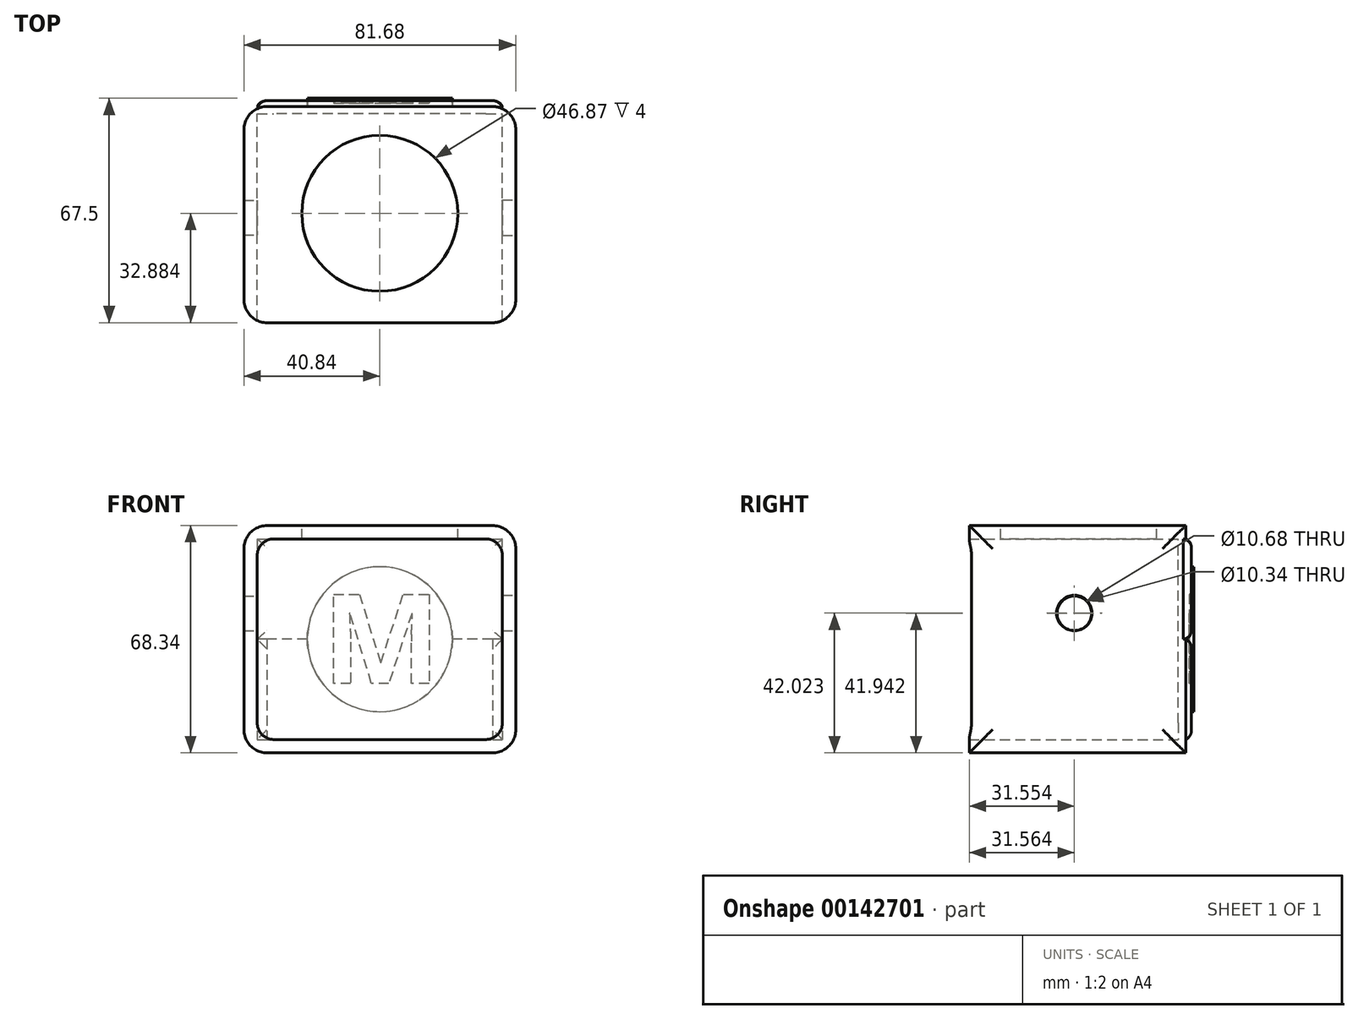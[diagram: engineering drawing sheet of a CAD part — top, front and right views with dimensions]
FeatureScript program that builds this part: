
annotation { "Feature Type Name" : "Feature", "Feature Type Description" : "" }
export const myFeature = defineFeature(function(context is Context, id is Id, definition is map)
    precondition{}
    {
        {
            var Q0;
            Q0=qCreatedBy(makeId("Front.planeOp"),FACE);
            var sketch = newSketch(context, id + "F0", { "sketchPlane" : qUnion([Q0])});
            skLineSegment(sketch, "E0.bottom", {"start": v(-40.84, 34.17) * mm, "end": v(40.84, 34.17) * mm});
            skLineSegment(sketch, "E0.top", {"start": v(-40.84, -34.17) * mm, "end": v(40.84, -34.17) * mm});
            skLineSegment(sketch, "E0.left", {"start": v(-40.84, 34.17) * mm, "end": v(-40.84, -34.17) * mm});
            skLineSegment(sketch, "E0.right", {"start": v(40.84, 34.17) * mm, "end": v(40.84, -34.17) * mm});
            skPoint(sketch, "E0.middle", {"position": v(0, 0) * mm});
            skText(sketch, "E1", { "text": "M", "fontName": "OpenSans-Bold.ttf"});
            skCircle(sketch, "E2", {"center": v(0, 0) * mm, "radius": 21.78 * mm});
            skLineSegment(sketch, "E3.0", {"start": v(-36.84, 30.17) * mm, "end": v(36.84, 30.17) * mm});
            skLineSegment(sketch, "E3.1", {"start": v(-36.84, 30.17) * mm, "end": v(-36.84, -30.17) * mm});
            skLineSegment(sketch, "E3.2", {"start": v(-36.84, -30.17) * mm, "end": v(36.84, -30.17) * mm});
            skLineSegment(sketch, "E3.3", {"start": v(36.84, 30.17) * mm, "end": v(36.84, -30.17) * mm});
            skLineSegment(sketch, "E4", {"start": v(36.84, 0) * mm, "end": v(21.78, 0) * mm});
            skLineSegment(sketch, "E5", {"start": v(-21.78, 0) * mm, "end": v(-36.84, 0) * mm});
            skLineSegment(sketch, "E6.0", {"start": v(36.3, 1.33) * mm, "end": v(21.78, 1.33) * mm});
            skLineSegment(sketch, "E7.MirrorCS", {"start": v(-36.3, 1.33) * mm, "end": v(-21.78, 1.33) * mm});
            skPoint(sketch, "E8", {"position": v(36.84, 0) * mm});
            skPoint(sketch, "E9", {"position": v(21.78, 0) * mm});
            const initialGuessF0  = {"E1": [-0.01722, -0.01329, 1, 0, 0.02702]};
            skSetInitialGuess(sketch, initialGuessF0);
            skSolve(sketch);
        }
        {
            var Q0;
            Q0=makeQuery(id+"F0.imprint","IMPRINT",FACE,{"disambiguationData":[TD([[makeQuery(id+"F0.imprint","IMPRINT",EDGE,{"derivedFrom":sQuery(id+"F0.wireOp",EDGE,"E1.sketch_text.stroke-0")}),1.0]])]});
            var Q1;
            Q1=makeQuery(id+"F0.imprint","IMPRINT",FACE,{"disambiguationData":[TD([[makeQuery(id+"F0.imprint","IMPRINT",EDGE,{"derivedFrom":sQuery(id+"F0.wireOp",EDGE,"E1.sketch_text.stroke-0")}),-1.0]])]});
            var Q2;
            {var subQ7=sQuery(id+"F0.wireOp",EDGE,"E0.bottom");Q2=makeQuery(id+"F0.imprint","IMPRINT",FACE,{"disambiguationData":[TD([[makeQuery(id+"F0.imprint","IMPRINT",EDGE,{"derivedFrom":subQ7}),-1.0]])]});}
            var Q3;
            {var subQ6=sQuery(id+"F0.wireOp",EDGE,"E0.top");Q3=makeQuery(id+"F0.imprint","IMPRINT",FACE,{"disambiguationData":[TD([[makeQuery(id+"F0.imprint","IMPRINT",EDGE,{"derivedFrom":subQ6}),1.0]])]});}
            var Q4;
            {var subQ0=sQuery(id+"F0.wireOp",EDGE,"E3.2");Q4=makeQuery(id+"F0.imprint","IMPRINT",FACE,{"disambiguationData":[TD([[makeQuery(id+"F0.imprint","IMPRINT",EDGE,{"derivedFrom":subQ0}),1.0]])]});}
            var Q5;
            {var subQ0=sQuery(id+"F0.wireOp",EDGE,"E3.0");Q5=makeQuery(id+"F0.imprint","IMPRINT",FACE,{"disambiguationData":[TD([[makeQuery(id+"F0.imprint","IMPRINT",EDGE,{"derivedFrom":subQ0}),-1.0]])]});}
            extrude(context, id + "F1", {"entities" : qUnion([Q0, Q1, Q2, Q3, Q4, Q5]), "depth" : 2.22 * mm});
        }
        {
            var Q0;
            Q0 = qSketchRegion(id + "F0", true);
            extrude(context, id + "F2", {"entities" : qUnion([Q0]), "operationType" : NewBodyOperationType.ADD, "depth" : 65 * mm});
        }
        {
            var Q0;
            Q0=makeQuery(id+"F0.imprint","IMPRINT",FACE,{"disambiguationData":[TD([[makeQuery(id+"F0.imprint","IMPRINT",EDGE,{"derivedFrom":sQuery(id+"F0.wireOp",EDGE,"E1.sketch_text.stroke-0")}),-1.0]])]});
            extrude(context, id + "F3", {"entities" : qUnion([Q0]), "operationType" : NewBodyOperationType.ADD, "oppositeDirection" : true, "depth" : 1 * mm});
        }
        {
            var Q0;
            Q0=makeQuery(id+"F0.imprint","IMPRINT",FACE,{"disambiguationData":[TD([[makeQuery(id+"F0.imprint","IMPRINT",EDGE,{"derivedFrom":sQuery(id+"F0.wireOp",EDGE,"E1.sketch_text.stroke-0")}),1.0]])]});
            extrude(context, id + "F4", {"entities" : qUnion([Q0]), "operationType" : NewBodyOperationType.ADD, "oppositeDirection" : true, "depth" : 2.5 * mm});
        }
        {
            var Q0;
            {var subQ3=sQuery(id+"F0.wireOp",EDGE,"E3.0");Q0=makeQuery(id+"F0.imprint","IMPRINT",FACE,{"disambiguationData":[TD([[makeQuery(id+"F0.imprint","IMPRINT",EDGE,{"derivedFrom":subQ3}),-1.0]])]});}
            var Q1;
            Q1=sQuery(id+"F0.wireOp",EDGE,"E4");
            var Q2;
            Q2=sQuery(id+"F0.wireOp",EDGE,"E5");
            extrude(context, id + "F5", {"entities" : qUnion([Q0]), "operationType" : NewBodyOperationType.ADD, "surfaceEntities" : qUnion([Q1, Q2]), "oppositeDirection" : true, "depth" : 1.75 * mm});
        }
        {
            var Q0;
            {var subQ0=sQuery(id+"F0.wireOp",EDGE,"E0.right");var subQ1=sQuery(id+"F0.wireOp",EDGE,"E0.bottom");Q0=makeQuery(id+"F2.boolean.opBoolean","MERGE",EDGE,{"derivedFrom":[makeQuery(id+"F1.opExtrude","SWEPT_EDGE",EDGE,{"disambiguationData":[OSD([subQ1,subQ0])]}),makeQuery(id+"F2.opExtrude","SWEPT_EDGE",EDGE,{"disambiguationData":[OSD([subQ1,subQ0])]})]});}
            var Q1;
            {var subQ0=sQuery(id+"F0.wireOp",EDGE,"E0.left");var subQ1=sQuery(id+"F0.wireOp",EDGE,"E0.bottom");Q1=makeQuery(id+"F2.boolean.opBoolean","MERGE",EDGE,{"derivedFrom":[makeQuery(id+"F1.opExtrude","SWEPT_EDGE",EDGE,{"disambiguationData":[OSD([subQ1,subQ0])]}),makeQuery(id+"F2.opExtrude","SWEPT_EDGE",EDGE,{"disambiguationData":[OSD([subQ1,subQ0])]})]});}
            var Q2;
            {var subQ0=sQuery(id+"F0.wireOp",EDGE,"E0.right");var subQ1=sQuery(id+"F0.wireOp",EDGE,"E0.top");Q2=makeQuery(id+"F2.boolean.opBoolean","MERGE",EDGE,{"derivedFrom":[makeQuery(id+"F1.opExtrude","SWEPT_EDGE",EDGE,{"disambiguationData":[OSD([subQ1,subQ0])]}),makeQuery(id+"F2.opExtrude","SWEPT_EDGE",EDGE,{"disambiguationData":[OSD([subQ1,subQ0])]})]});}
            var Q3;
            {var subQ0=sQuery(id+"F0.wireOp",EDGE,"E0.left");var subQ1=sQuery(id+"F0.wireOp",EDGE,"E0.top");Q3=makeQuery(id+"F2.boolean.opBoolean","MERGE",EDGE,{"derivedFrom":[makeQuery(id+"F1.opExtrude","SWEPT_EDGE",EDGE,{"disambiguationData":[OSD([subQ1,subQ0])]}),makeQuery(id+"F2.opExtrude","SWEPT_EDGE",EDGE,{"disambiguationData":[OSD([subQ1,subQ0])]})]});}
            var Q4;
            Q4=makeQuery(id+"F1.opExtrude","CAP_EDGE",EDGE,{"disambiguationData":[OSD([sQuery(id+"F0.wireOp",EDGE,"E0.left")])],"isStart":true});
            var Q5;
            Q5=makeQuery(id+"F2.opExtrude","CAP_EDGE",EDGE,{"disambiguationData":[OSD([sQuery(id+"F0.wireOp",EDGE,"E0.left")])],"isStart":false});
            var Q6;
            Q6=makeQuery(id+"F1.opExtrude","CAP_EDGE",EDGE,{"disambiguationData":[OSD([sQuery(id+"F0.wireOp",EDGE,"E0.right")])],"isStart":true});
            var Q7;
            Q7=makeQuery(id+"F2.opExtrude","CAP_EDGE",EDGE,{"disambiguationData":[OSD([sQuery(id+"F0.wireOp",EDGE,"E0.right")])],"isStart":false});
            fillet(context, id + "F6", {"entities" : qUnion([Q0, Q1, Q2, Q3, Q4, Q5, Q6, Q7]), "radius" : 6.96 * mm, "tangentPropagation" : true, "allowEdgeOverflow" : false});
        }
        {
            var Q0;
            Q0=makeQuery(id+"F5.opExtrude","CAP_EDGE",EDGE,{"disambiguationData":[OSD([sQuery(id+"F0.wireOp",EDGE,"E3.3")])],"isStart":false});
            var Q1;
            Q1=makeQuery(id+"F5.opExtrude","CAP_EDGE",EDGE,{"disambiguationData":[OSD([sQuery(id+"F0.wireOp",EDGE,"E3.1")])],"isStart":false});
            var Q2;
            Q2=makeQuery(id+"F5.opExtrude","CAP_EDGE",EDGE,{"disambiguationData":[OSD([sQuery(id+"F0.wireOp",EDGE,"E3.0")])],"isStart":false});
            var Q3;
            Q3=makeQuery(id+"F5.opExtrude","CAP_EDGE",EDGE,{"disambiguationData":[OSD([sQuery(id+"F0.wireOp",EDGE,"E4")])],"isStart":false});
            var Q4;
            Q4=makeQuery(id+"F5.opExtrude","CAP_EDGE",EDGE,{"disambiguationData":[OSD([sQuery(id+"F0.wireOp",EDGE,"E5")])],"isStart":false});
            fillet(context, id + "F7", {"entities" : qUnion([Q0, Q1, Q2, Q3, Q4]), "radius" : 3 * mm, "tangentPropagation" : true, "allowEdgeOverflow" : false});
        }
        {
            var Q0;
            {var subQ0=sQuery(id+"F0.wireOp",EDGE,"E0.bottom");Q0=makeQuery(id+"F2.boolean.opBoolean","MERGE",FACE,{"derivedFrom":[makeQuery(id+"F1.opExtrude","SWEPT_FACE",FACE,{"disambiguationData":[OSD([subQ0])]}),makeQuery(id+"F2.opExtrude","SWEPT_FACE",FACE,{"disambiguationData":[OSD([subQ0])]})]});}
            var sketch = newSketch(context, id + "F8", { "sketchPlane" : qUnion([Q0])});
            skCircle(sketch, "E10", {"center": v(0, -32.12) * mm, "radius": 23.43 * mm});
            skSolve(sketch);
        }
        {
            var Q0;
            Q0=makeQuery(id+"F8.imprint","IMPRINT",FACE,{"disambiguationData":[TD([[makeQuery(id+"F8.imprint","IMPRINT",EDGE,{"derivedFrom":sQuery(id+"F8.wireOp",EDGE,"E10")}),1.0]])]});
            var Q1;
            Q1=sQuery(id+"F8.wireOp",EDGE,"E10");
            extrude(context, id + "F9", {"entities" : qUnion([Q0]), "operationType" : NewBodyOperationType.REMOVE, "surfaceEntities" : qUnion([Q1]), "oppositeDirection" : true, "depth" : 25 * mm});
        }
        {
            var Q0;
            Q0=makeQuery(id+"F2.opExtrude","SWEPT_EDGE",EDGE,{"disambiguationData":[OSD([sQuery(id+"F0.wireOp",EDGE,"E3.0"),sQuery(id+"F0.wireOp",EDGE,"E3.1")])]});
            var Q1;
            Q1=makeQuery(id+"F2.opExtrude","SWEPT_EDGE",EDGE,{"disambiguationData":[OSD([sQuery(id+"F0.wireOp",EDGE,"E3.0"),sQuery(id+"F0.wireOp",EDGE,"E3.3")])]});
            var Q2;
            Q2=makeQuery(id+"F2.opExtrude","SWEPT_EDGE",EDGE,{"disambiguationData":[OSD([sQuery(id+"F0.wireOp",EDGE,"E3.2"),sQuery(id+"F0.wireOp",EDGE,"E3.3")])]});
            var Q3;
            Q3=makeQuery(id+"F2.opExtrude","SWEPT_EDGE",EDGE,{"disambiguationData":[OSD([sQuery(id+"F0.wireOp",EDGE,"E3.1"),sQuery(id+"F0.wireOp",EDGE,"E3.2")])]});
            fillet(context, id + "F10", {"entities" : qUnion([Q0, Q1, Q2, Q3]), "radius" : 5 * mm, "tangentPropagation" : true, "allowEdgeOverflow" : false});
        }
        {
            var Q0;
            {var subQ1=sQuery(id+"F0.wireOp",EDGE,"E3.2");Q0=makeQuery(id+"F0.imprint","IMPRINT",FACE,{"disambiguationData":[TD([[makeQuery(id+"F0.imprint","IMPRINT",EDGE,{"derivedFrom":subQ1}),1.0]])]});}
            extrude(context, id + "F11", {"entities" : qUnion([Q0]), "operationType" : NewBodyOperationType.ADD, "oppositeDirection" : true, "depth" : 1.75 * mm});
        }
        {
            var Q0;
            Q0=makeQuery(id+"F11.opExtrude","CAP_EDGE",EDGE,{"disambiguationData":[OSD([sQuery(id+"F0.wireOp",EDGE,"E3.3")])],"isStart":false});
            var Q1;
            Q1=makeQuery(id+"F11.opExtrude","CAP_EDGE",EDGE,{"disambiguationData":[OSD([sQuery(id+"F0.wireOp",EDGE,"E4")])],"isStart":false});
            var Q2;
            Q2=makeQuery(id+"F11.opExtrude","CAP_EDGE",EDGE,{"disambiguationData":[OSD([sQuery(id+"F0.wireOp",EDGE,"E5")])],"isStart":false});
            var Q3;
            Q3=makeQuery(id+"F11.opExtrude","CAP_EDGE",EDGE,{"disambiguationData":[OSD([sQuery(id+"F0.wireOp",EDGE,"E3.1")])],"isStart":false});
            var Q4;
            Q4=makeQuery(id+"F11.opExtrude","CAP_EDGE",EDGE,{"disambiguationData":[OSD([sQuery(id+"F0.wireOp",EDGE,"E3.2")])],"isStart":false});
            fillet(context, id + "F12", {"entities" : qUnion([Q0, Q1, Q2, Q3, Q4]), "radius" : 3 * mm, "tangentPropagation" : true, "allowEdgeOverflow" : false});
        }
        {
            var Q0;
            {var subQ0=sQuery(id+"F0.wireOp",EDGE,"E0.right");Q0=makeQuery(id+"F2.boolean.opBoolean","MERGE",FACE,{"derivedFrom":[makeQuery(id+"F1.opExtrude","SWEPT_FACE",FACE,{"disambiguationData":[OSD([subQ0])]}),makeQuery(id+"F2.opExtrude","SWEPT_FACE",FACE,{"disambiguationData":[OSD([subQ0])]})]});}
            var sketch = newSketch(context, id + "F13", { "sketchPlane" : qUnion([Q0])});
            skPoint(sketch, "E11", {"position": v(-128.87, 15.32) * mm});
            skCircle(sketch, "E12", {"center": v(-33.45, 7.85) * mm, "radius": 5.34 * mm});
            skSolve(sketch);
        }
        {
            var Q0;
            Q0=makeQuery(id+"F13.imprint","IMPRINT",FACE,{"disambiguationData":[TD([[makeQuery(id+"F13.imprint","IMPRINT",EDGE,{"derivedFrom":sQuery(id+"F13.wireOp",EDGE,"E12")}),1.0]])]});
            extrude(context, id + "F14", {"entities" : qUnion([Q0]), "operationType" : NewBodyOperationType.REMOVE, "oppositeDirection" : true, "depth" : 25 * mm});
        }
        {
            var Q0;
            Q0=makeQuery(id+"F2.opExtrude","SWEPT_FACE",FACE,{"disambiguationData":[OSD([sQuery(id+"F0.wireOp",EDGE,"E3.1")])]});
            var sketch = newSketch(context, id + "F15", { "sketchPlane" : qUnion([Q0])});
            skCircle(sketch, "E13", {"center": v(-33.44, 7.77) * mm, "radius": 5.17 * mm});
            skSolve(sketch);
        }
        {
            var Q0;
            Q0 = qSketchRegion(id + "F15", true);
            extrude(context, id + "F16", {"entities" : qUnion([Q0]), "operationType" : NewBodyOperationType.REMOVE, "oppositeDirection" : true, "depth" : 25 * mm});
        }
    });
